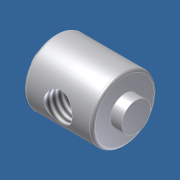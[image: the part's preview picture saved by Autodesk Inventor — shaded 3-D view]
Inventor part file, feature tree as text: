
AUTODESK INVENTOR PART (.ipt)
format: ipt  version: unknown  size: 214,016 bytes
history: native  units: in
note: dims shown in document units (in); Inventor stores cm internally (conversion verified against a paired STEP export)
features: sketch x2, revolve x1, fillet x1, plane x1, hole x1
ambient origin geometry x8: Origin, YZ Plane, XZ Plane, XY Plane, X Axis, Y Axis, Z Axis, Center Point
bodies: Solid1 (feature_tree)
feature tree (6):
  revolve  "Revolution1"  [1 undecoded]
  fillet  "Fillet1"  Radius=0.125in
  plane  "Work Plane1"
  hole  "Hole1"  [1 undecoded]
  sketch  "Sketch1"  dims[d0=0.1562in d1=0.1562in d2=0.125in]
  sketch  "Sketch2"  dims[d3=0.125in d4=1.0in d5=0.35in d6=90.0deg d7=0.0312in d8=0.307in d9=0.75in d10=0.375in d11=0.25in d12=0.5635in d13=1.0in d14=0.8108in]
note: 2 required parameter values undecoded (feature->parameter linkage not recoverable at this tier; creation-order binding heuristic only, values carry confidence <= 0.55)